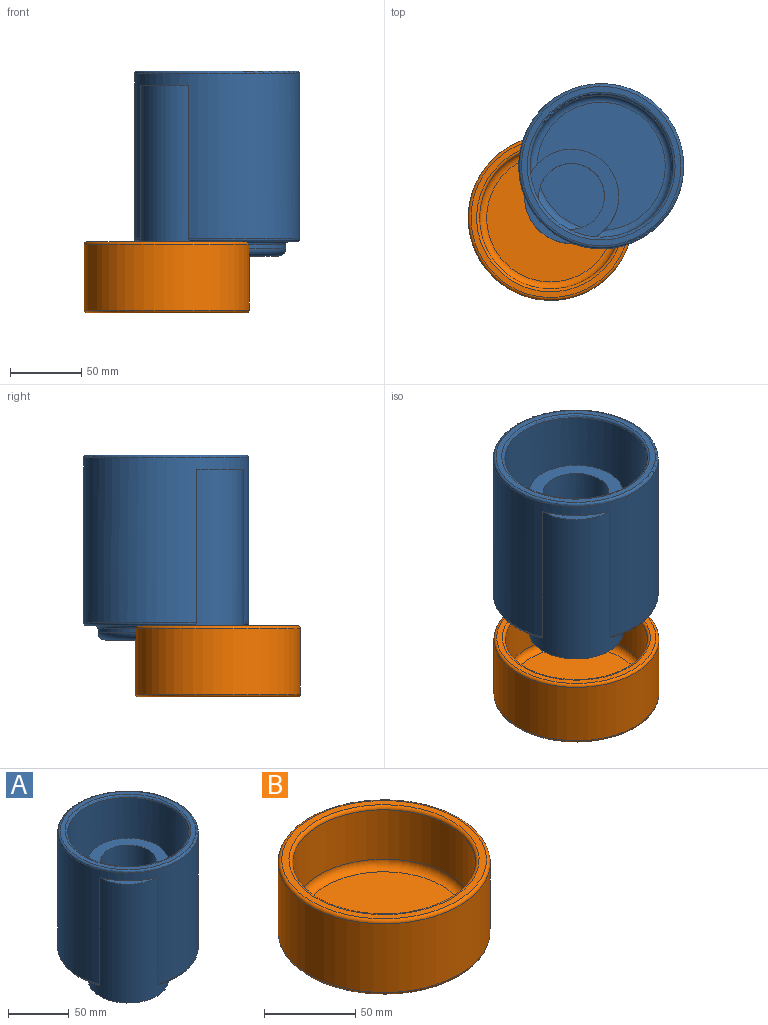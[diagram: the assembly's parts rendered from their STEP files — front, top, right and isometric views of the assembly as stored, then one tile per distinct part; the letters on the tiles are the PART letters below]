
ASSEMBLY  parts=2 mates=1
PART A: 25 faces, bbox 125.6x125.6x130 mm
  f0: plane 45.09x44.95mm, normal (0,0,1), area 1438.3mm2, adj f5,f19
  f1: plane 20.4x20.02mm, normal (0,0,-1), area 56.5mm2, adj f3,f23
  f2: cylinder r=48mm len=25.26mm, axis (0,0,1), area 108.8mm2, adj f3,f17,f23
  f3: torus R=50mm, axis (0,0,1), area 106.2mm2, adj f1,f2,f23
  f4: torus R=43mm, axis (0,0,-1), area 1702.3mm2, adj f11,f12,f22
  f5: torus R=45mm, axis (0,0,1), area 275.2mm2, adj f0,f6,f19
  f6: cylinder r=50mm len=103mm, axis (0,0,-1), area 28524.6mm2, adj f5,f15,f18,f19,f20,f21
  f7: cylinder r=58mm len=116mm, axis (0,0,-1), area 37024.3mm2, adj f14,f16,f22,f24
  f8: plane 112x112mm, normal (0,0,1), area 1357.2mm2, adj f15,f16
  f9: plane 89.98x89.94mm, normal (0,0,1), area 3923.1mm2, adj f18,f20
  f10: plane 112x112mm, normal (0,0,-1), area 1617mm2, adj f13,f14,f22
  f11: cylinder r=48mm len=96mm, axis (0,0,1), area 689.1mm2, adj f4,f13,f22
  f12: plane 97.35x96.95mm, normal (0,0,-1), area 6636.3mm2, adj f4,f17,f22,f23
  f13: torus R=50mm, axis (0,0,1), area 738.7mm2, adj f10,f11,f22
  f14: torus R=56mm, axis (0,0,1), area 969mm2, adj f7,f10,f22
  f15: torus R=52mm, axis (0,0,1), area 1001.3mm2, adj f6,f8
  f16: torus R=56mm, axis (0,0,1), area 1130.5mm2, adj f7,f8
  f17: torus R=43mm, axis (0,0,-1), area 317.5mm2, adj f2,f12,f23
  f18: torus R=45mm, axis (0,0,1), area 1816.3mm2, adj f6,f9,f20
  f19: cylinder r=23.13mm len=100mm, axis (0,0,-1), area 11425.4mm2, adj f0,f5,f6,f21
  f20: cylinder r=33.13mm len=100mm, axis (0,0,-1), area 12154.9mm2, adj f6,f9,f18,f21
  f21: plane 62.05x61.74mm, normal (0,0,1), area 1175.8mm2, adj f6,f19,f20
  f22: cylinder r=33.13mm len=120mm, axis (0,0,-1), area 6728mm2, adj f4,f7,f10,f11,f12,f13,f14,f24
  f23: cylinder r=23.13mm len=33.74mm, axis (0,0,-1), area 420mm2, adj f1,f2,f3,f12,f17
  f24: plane 33.68x33.06mm, normal (0,0,1), area 162.1mm2, adj f7,f22
PART B: 9 faces, bbox 125.6x125.6x50 mm
  f0: plane 90x90mm, normal (0,0,1), area 6361.7mm2, adj f5
  f1: cylinder r=50mm len=100mm, axis (0,0,-1), area 10367.3mm2, adj f5,f7
  f2: cylinder r=58mm len=116mm, axis (0,0,-1), area 16763.5mm2, adj f6,f8
  f3: plane 112x112mm, normal (0,0,1), area 1357.2mm2, adj f7,f8
  f4: plane 112x112mm, normal (0,0,-1), area 9852mm2, adj f6
  f5: torus R=45mm, axis (0,0,1), area 2377.7mm2, adj f0,f1
  f6: torus R=56mm, axis (0,0,1), area 1130.5mm2, adj f2,f4
  f7: torus R=52mm, axis (0,0,1), area 1001.3mm2, adj f1,f3
  f8: torus R=56mm, axis (0,0,1), area 1130.5mm2, adj f2,f3
PLACE A t=(-7.43,21.35,-6.54)mm
PLACE B t=(-42.96,-14.85,-66.54)mm
MATE fastened B.f2 <-> A.f1  axis (0,0,1) through (-42.96,-14.85,-16.54)mm
